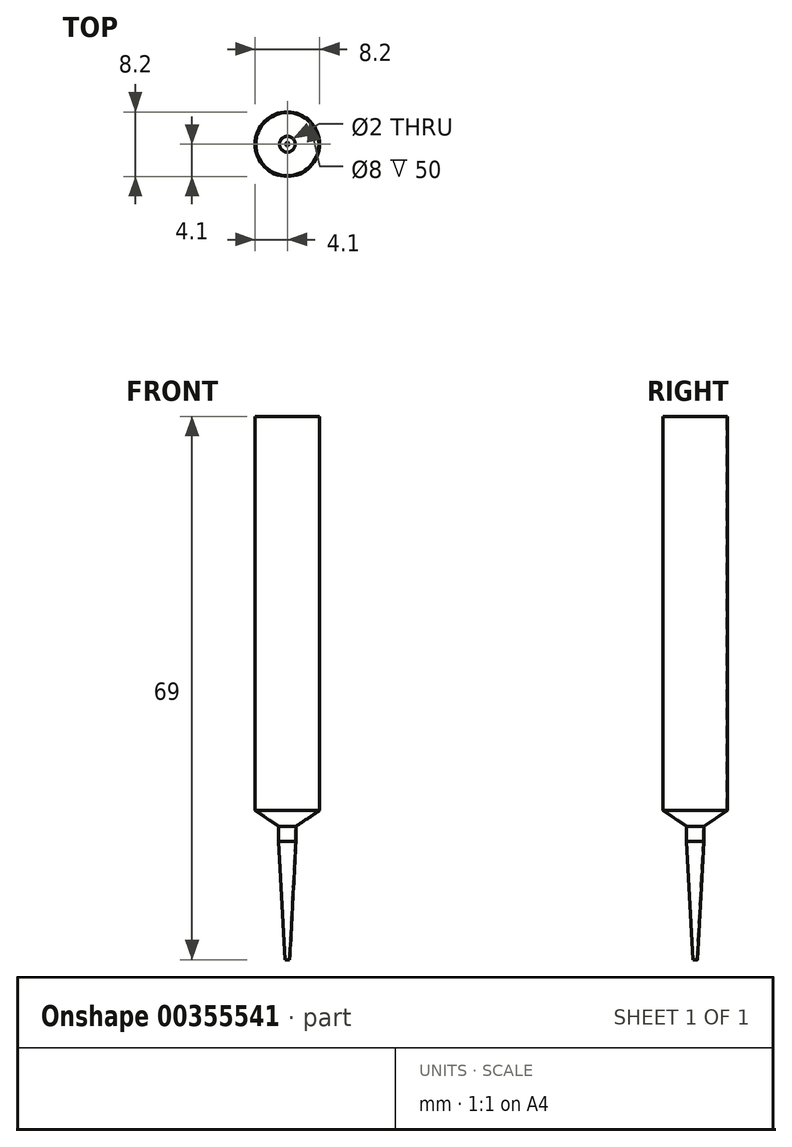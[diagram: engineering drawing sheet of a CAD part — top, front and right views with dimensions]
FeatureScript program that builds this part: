
annotation { "Feature Type Name" : "Feature", "Feature Type Description" : "" }
export const myFeature = defineFeature(function(context is Context, id is Id, definition is map)
    precondition{}
    {
        {
            var Q0;
            Q0=qCreatedBy(makeId("Front.planeOp"),FACE);
            var sketch = newSketch(context, id + "F0", { "sketchPlane" : qUnion([Q0])});
            skLineSegment(sketch, "E0", {"start": v(4, 0) * mm, "end": v(4, -50) * mm});
            skLineSegment(sketch, "E1", {"start": v(-4, 0) * mm, "end": v(-4, -50) * mm});
            skLineSegment(sketch, "E2", {"start": v(-4, -50) * mm, "end": v(-1, -52) * mm});
            skLineSegment(sketch, "E3", {"start": v(4, -50) * mm, "end": v(1, -52) * mm});
            skLineSegment(sketch, "E4", {"start": v(-1, -52) * mm, "end": v(-1, -54) * mm});
            skLineSegment(sketch, "E5", {"start": v(1, -52) * mm, "end": v(1, -54) * mm});
            skLineSegment(sketch, "E6", {"start": v(-1, -54) * mm, "end": v(-0.2, -69) * mm});
            skLineSegment(sketch, "E7", {"start": v(1, -54) * mm, "end": v(0.2, -69) * mm});
            skLineSegment(sketch, "E8", {"start": v(0, 0) * mm, "end": v(0, -69) * mm});
            skLineSegment(sketch, "E9", {"start": v(-4.1, 0) * mm, "end": v(-4.1, -50.05) * mm});
            skLineSegment(sketch, "E10", {"start": v(-4.1, -50.05) * mm, "end": v(-1.1, -52.05) * mm});
            skLineSegment(sketch, "E11", {"start": v(-1.1, -52.05) * mm, "end": v(-1.1, -54) * mm});
            skLineSegment(sketch, "E12", {"start": v(-1.1, -54) * mm, "end": v(-0.3, -69) * mm});
            skLineSegment(sketch, "E13", {"start": v(-0.3, -69) * mm, "end": v(-0.2, -69) * mm});
            skLineSegment(sketch, "E14", {"start": v(-4.1, 0) * mm, "end": v(-4, 0) * mm});
            skSolve(sketch);
        }
        {
            var Q0;
            Q0=makeQuery(id+"F0.imprint","IMPRINT",FACE,{"disambiguationData":[TD([[makeQuery(id+"F0.imprint","IMPRINT",EDGE,{"derivedFrom":sQuery(id+"F0.wireOp",EDGE,"E1")}),-1.0]])]});
            var Q1;
            Q1=sQuery(id+"F0.wireOp",EDGE,"E1");
            var Q2;
            Q2=sQuery(id+"F0.wireOp",EDGE,"E2");
            var Q3;
            Q3=sQuery(id+"F0.wireOp",EDGE,"E4");
            var Q4;
            Q4=sQuery(id+"F0.wireOp",EDGE,"E6");
            var Q5;
            Q5=sQuery(id+"F0.wireOp",EDGE,"E8");
            revolve(context, id + "F1", {"entities" : qUnion([Q0]), "surfaceEntities" : qUnion([Q1, Q2, Q3, Q4]), "axis" : qUnion([Q5]), "revolveType" : RevolveType.FULL});
        }
    });
